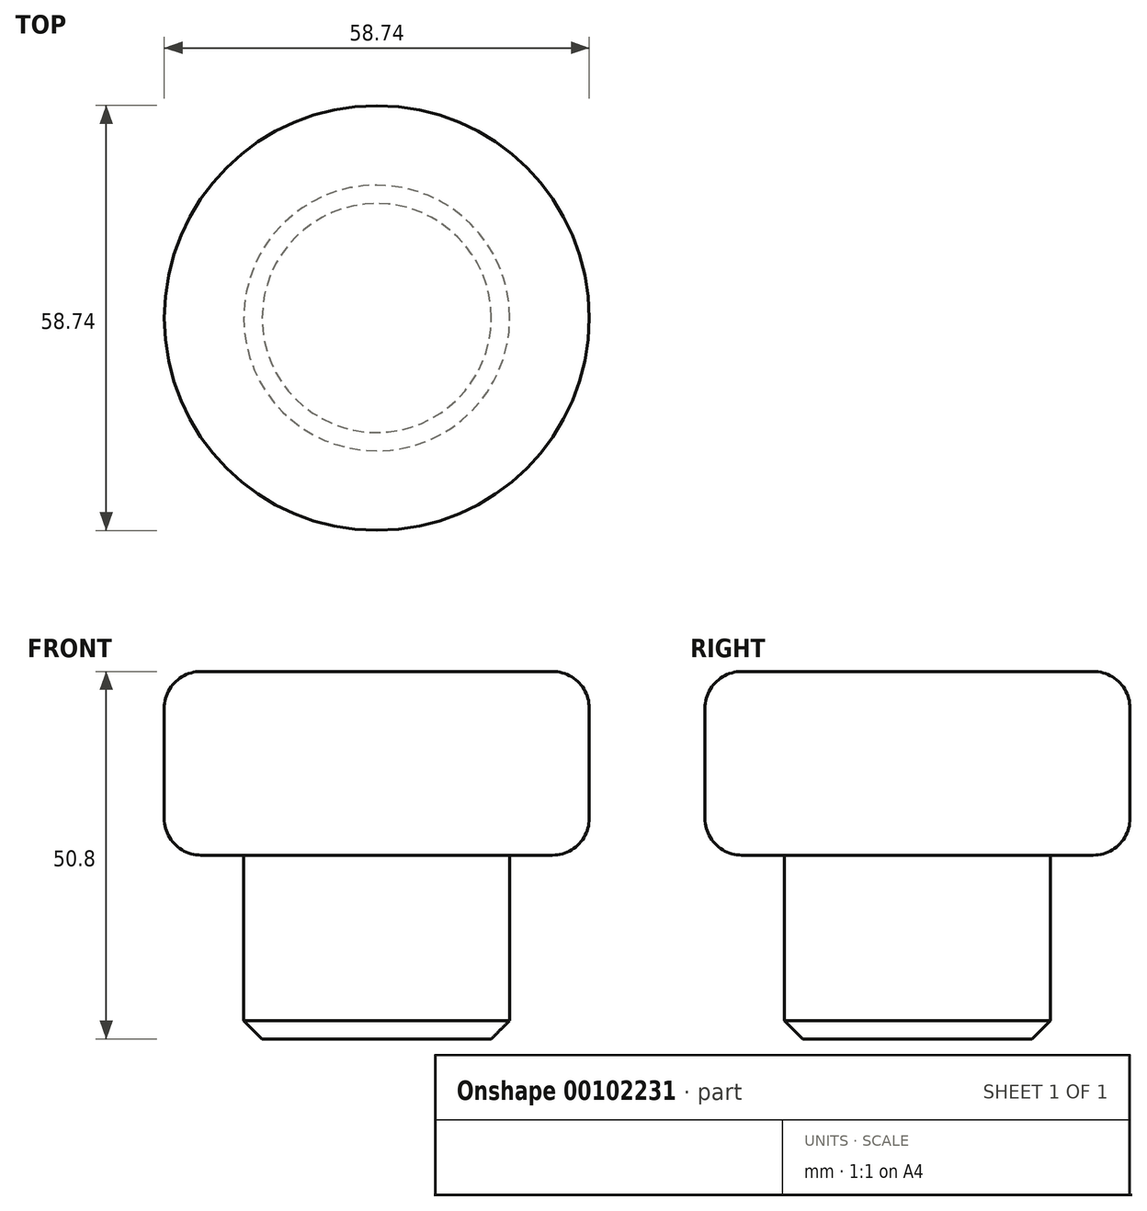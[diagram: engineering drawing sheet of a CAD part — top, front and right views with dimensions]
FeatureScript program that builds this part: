
annotation { "Feature Type Name" : "Feature", "Feature Type Description" : "" }
export const myFeature = defineFeature(function(context is Context, id is Id, definition is map)
    precondition{}
    {
        {
            var Q0;
            Q0=qCreatedBy(makeId("Top.planeOp"),FACE);
            var sketch = newSketch(context, id + "F0", { "sketchPlane" : qUnion([Q0])});
            skCircle(sketch, "E0", {"center": v(0, 0) * mm, "radius": 18.37 * mm});
            skSolve(sketch);
        }
        {
            var Q0;
            Q0=makeQuery(id+"F0.imprint","IMPRINT",FACE,{"disambiguationData":[TD([[makeQuery(id+"F0.imprint","IMPRINT",EDGE,{"derivedFrom":sQuery(id+"F0.wireOp",EDGE,"E0")}),1.0]])]});
            extrude(context, id + "F1", {"entities" : qUnion([Q0]), "oppositeDirection" : true, "depth" : 25.4 * mm});
        }
        {
            var Q0;
            Q0=qCreatedBy(makeId("Top.planeOp"),FACE);
            var sketch = newSketch(context, id + "F2", { "sketchPlane" : qUnion([Q0])});
            skCircle(sketch, "E1", {"center": v(0, 0) * mm, "radius": 29.37 * mm});
            skSolve(sketch);
        }
        {
            var Q0;
            Q0=makeQuery(id+"F2.imprint","IMPRINT",FACE,{"disambiguationData":[TD([[makeQuery(id+"F2.imprint","IMPRINT",EDGE,{"derivedFrom":sQuery(id+"F2.wireOp",EDGE,"E1")}),1.0]])]});
            extrude(context, id + "F3", {"entities" : qUnion([Q0]), "operationType" : NewBodyOperationType.ADD, "depth" : 25.4 * mm});
        }
        {
            var Q0;
            Q0=makeQuery(id+"F3.opExtrude","CAP_EDGE",EDGE,{"disambiguationData":[OSD([sQuery(id+"F2.wireOp",EDGE,"E1")])],"isStart":false});
            fillet(context, id + "F4", {"entities" : qUnion([Q0]), "radius" : 5.08 * mm, "tangentPropagation" : true, "allowEdgeOverflow" : false});
        }
        {
            var Q0;
            Q0=makeQuery(id+"F3.opExtrude","CAP_EDGE",EDGE,{"disambiguationData":[OSD([sQuery(id+"F2.wireOp",EDGE,"E1")])],"isStart":true});
            fillet(context, id + "F5", {"entities" : qUnion([Q0]), "radius" : 5.08 * mm, "tangentPropagation" : true, "allowEdgeOverflow" : false});
        }
        {
            var Q0;
            Q0=makeQuery(id+"F1.opExtrude","CAP_EDGE",EDGE,{"disambiguationData":[OSD([sQuery(id+"F0.wireOp",EDGE,"E0")])],"isStart":false});
            chamfer(context, id + "F6", {"entities" : qUnion([Q0]), "width" : 2.54 * mm, "tangentPropagation" : true});
        }
    });
